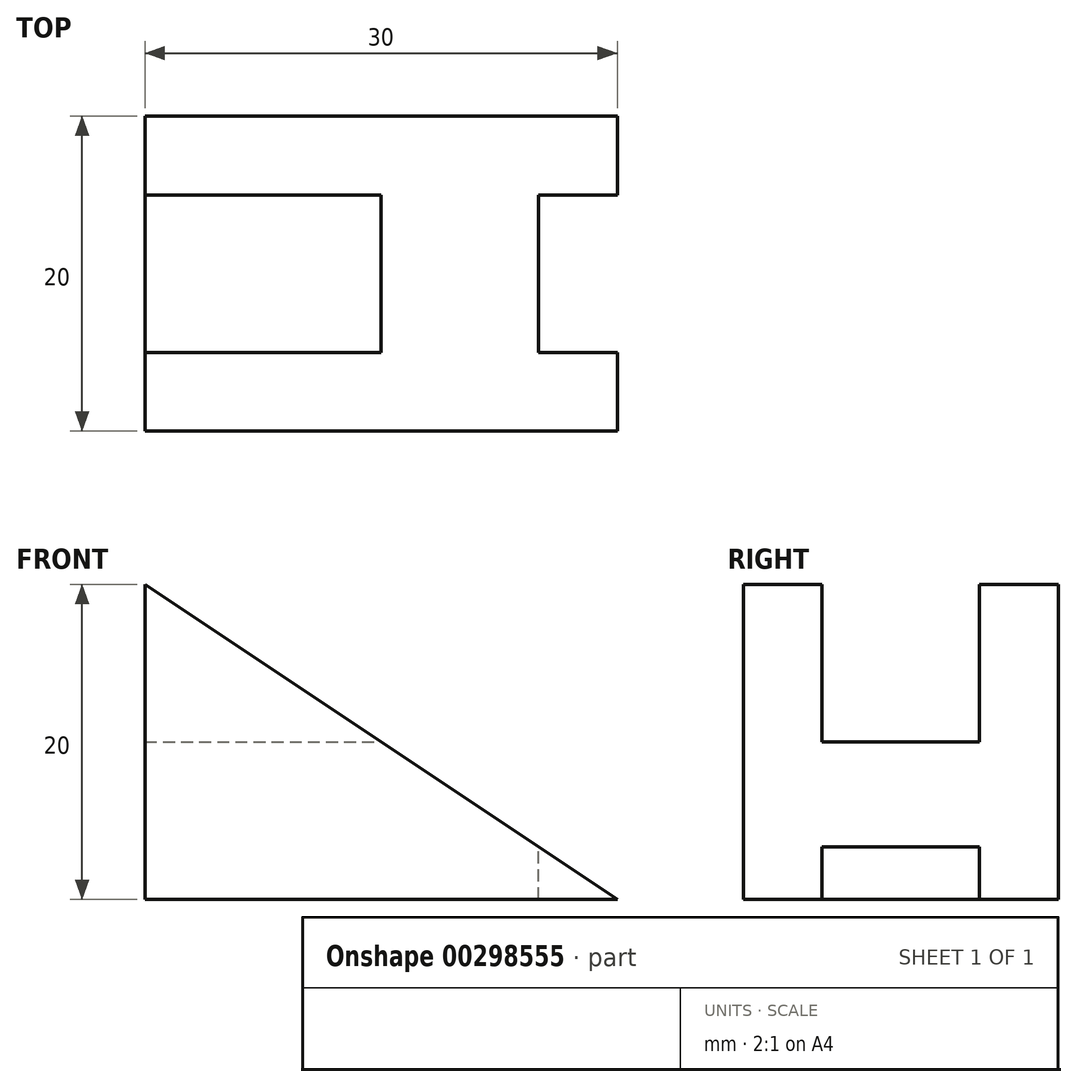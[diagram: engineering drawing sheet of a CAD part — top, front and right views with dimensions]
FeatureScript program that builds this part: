
annotation { "Feature Type Name" : "Feature", "Feature Type Description" : "" }
export const myFeature = defineFeature(function(context is Context, id is Id, definition is map)
    precondition{}
    {
        {
            var Q0;
            Q0=qCreatedBy(makeId("Front.planeOp"),FACE);
            var sketch = newSketch(context, id + "F0", { "sketchPlane" : qUnion([Q0])});
            skLineSegment(sketch, "E0.bottom", {"start": v(0, 0) * mm, "end": v(30, 0) * mm});
            skLineSegment(sketch, "E0.top", {"start": v(0, 20) * mm, "end": v(30, 20) * mm});
            skLineSegment(sketch, "E0.left", {"start": v(0, 0) * mm, "end": v(0, 20) * mm});
            skLineSegment(sketch, "E0.right", {"start": v(30, 0) * mm, "end": v(30, 20) * mm});
            skSolve(sketch);
        }
        {
            var Q0;
            Q0 = qSketchRegion(id + "F0", true);
            extrude(context, id + "F1", {"entities" : qUnion([Q0]), "depth" : 20 * mm});
        }
        {
            var Q0;
            Q0=makeQuery(id+"F1.opExtrude","SWEPT_FACE",FACE,{"disambiguationData":[OSD([sQuery(id+"F0.wireOp",EDGE,"E0.top")])]});
            var sketch = newSketch(context, id + "F2", { "sketchPlane" : qUnion([Q0])});
            skLineSegment(sketch, "E1.bottom", {"start": v(30, -5) * mm, "end": v(25, -5) * mm});
            skLineSegment(sketch, "E1.top", {"start": v(30, -15) * mm, "end": v(25, -15) * mm});
            skLineSegment(sketch, "E1.left", {"start": v(30, -5) * mm, "end": v(30, -15) * mm});
            skLineSegment(sketch, "E1.right", {"start": v(25, -5) * mm, "end": v(25, -15) * mm});
            skSolve(sketch);
        }
        {
            var Q0;
            Q0 = qSketchRegion(id + "F2", true);
            extrude(context, id + "F3", {"entities" : qUnion([Q0]), "operationType" : NewBodyOperationType.REMOVE, "endBound" : BoundingType.THROUGH_ALL, "oppositeDirection" : true, "depth" : 25 * mm});
        }
        {
            var Q0;
            Q0=makeQuery(id+"F3.boolean.opBoolean","COPY",FACE,{"derivedFrom":makeQuery(id+"F3.opExtrude","SWEPT_FACE",FACE,{"disambiguationData":[OSD([sQuery(id+"F2.wireOp",EDGE,"E1.right")])]})});
            var sketch = newSketch(context, id + "F4", { "sketchPlane" : qUnion([Q0])});
            skLineSegment(sketch, "E2.bottom", {"start": v(-15, 20) * mm, "end": v(-5, 20) * mm});
            skLineSegment(sketch, "E2.top", {"start": v(-15, 10) * mm, "end": v(-5, 10) * mm});
            skLineSegment(sketch, "E2.left", {"start": v(-15, 20) * mm, "end": v(-15, 10) * mm});
            skLineSegment(sketch, "E2.right", {"start": v(-5, 20) * mm, "end": v(-5, 10) * mm});
            skSolve(sketch);
        }
        {
            var Q0;
            Q0 = qSketchRegion(id + "F4", true);
            extrude(context, id + "F5", {"entities" : qUnion([Q0]), "operationType" : NewBodyOperationType.REMOVE, "endBound" : BoundingType.THROUGH_ALL, "oppositeDirection" : true, "depth" : 25 * mm});
        }
        {
            var Q0;
            Q0=makeQuery(id+"F1.opExtrude","CAP_FACE",FACE,{"disambiguationData":[OSD([sQuery(id+"F0.wireOp",EDGE,"E0.bottom"),sQuery(id+"F0.wireOp",EDGE,"E0.top"),sQuery(id+"F0.wireOp",EDGE,"E0.left"),sQuery(id+"F0.wireOp",EDGE,"E0.right")])],"isStart":false});
            var sketch = newSketch(context, id + "F6", { "sketchPlane" : qUnion([Q0])});
            skLineSegment(sketch, "E3", {"start": v(0, 20) * mm, "end": v(30, 0) * mm});
            skLineSegment(sketch, "E4", {"start": v(30, 0) * mm, "end": v(30, 20) * mm});
            skLineSegment(sketch, "E5", {"start": v(30, 20) * mm, "end": v(0, 20) * mm});
            skSolve(sketch);
        }
        {
            var Q0;
            Q0 = qSketchRegion(id + "F6", true);
            extrude(context, id + "F7", {"entities" : qUnion([Q0]), "operationType" : NewBodyOperationType.REMOVE, "oppositeDirection" : true, "depth" : 25 * mm});
        }
    });
